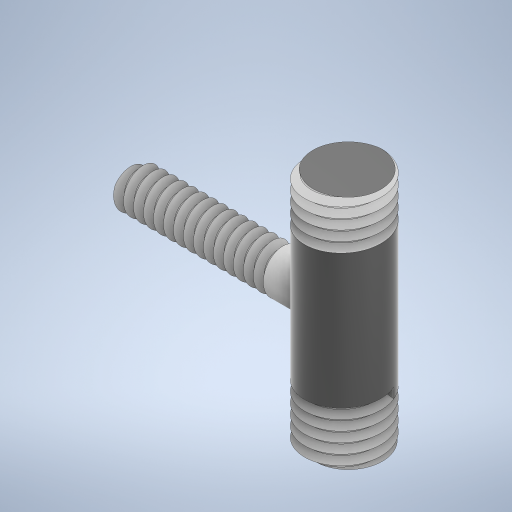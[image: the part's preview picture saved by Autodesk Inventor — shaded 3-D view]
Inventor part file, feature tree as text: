
AUTODESK INVENTOR PART (.ipt)
format: ipt  version: 2024 (Build 280153000, 153)  size: 687,616 bytes
history: native  units: mm
features: sketch x5, helix x3, extrude x2, plane x1
ambient origin geometry x8: Origin, YZ Plane, XZ Plane, XY Plane, X Axis, Y Axis, Z Axis, Center Point
bodies: Solid1 (feature_tree)
feature tree (11):
  extrude  "Extrusion1"  Depth=40.0mm TaperAngle=0.0deg
  plane  "Work Plane1"
  extrude  "Extrusion3"  Depth=1.7mm TaperAngle=0.0deg
  helix  "Coil1"  [1 undecoded]
  helix  "Coil2"  [1 undecoded]
  helix  "Coil3"  [1 undecoded]
  sketch  "Sketch1"  dims[d0=13.0mm d1=40.0mm d2=0.0mm]
  sketch  "Sketch4"  dims[d9=7.0mm d10=40.0mm d11=0.0mm d12=2.0mm d13=1.7mm d14=60.0deg]
  sketch  "Sketch5"  dims[d15=0.2mm]
  sketch  "Sketch6"  dims[d16=1.7mm d17=28.0mm d18=10.0mm d19=0.0mm d20=90.0deg d21=90.0deg d22=0.0mm d23=0.0mm]
  sketch  "Sketch7"  dims[d24=1.7mm d25=60.0deg d26=0.2mm d27=1.7mm d28=15.0mm d29=10.0mm d30=0.0mm d31=90.0deg d32=90.0deg d33=0.0mm d34=0.0mm d35=2.0mm d36=1.7mm d37=60.0deg d38=0.2mm d39=1.7mm d40=12.0mm d41=10.0mm d42=0.0mm d43=90.0deg d44=90.0deg d45=0.0mm d46=0.0mm]
note: 3 required parameter values undecoded (feature->parameter linkage not recoverable at this tier; creation-order binding heuristic only, values carry confidence <= 0.55)
